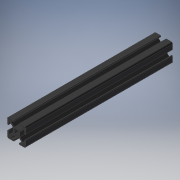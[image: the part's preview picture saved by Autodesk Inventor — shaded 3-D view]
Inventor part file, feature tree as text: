
AUTODESK INVENTOR PART (.ipt)
format: ipt  version: 2025 (Build 290162000, 162)  size: 238,080 bytes
history: native  units: mm
features: extrude x1, sketch x1
ambient origin geometry x8: Origin, YZ Plane, XZ Plane, XY Plane, X Axis, Y Axis, Z Axis, Center Point
bodies: Solid1 (feature_tree)
feature tree (2):
  extrude  "Extrusion1"  [1 undecoded]
  sketch  "Sketch_1"  dims[d0=160.0mm d1=0.0mm]
note: 1 required parameter value undecoded (feature->parameter linkage not recoverable at this tier; creation-order binding heuristic only, values carry confidence <= 0.55)
